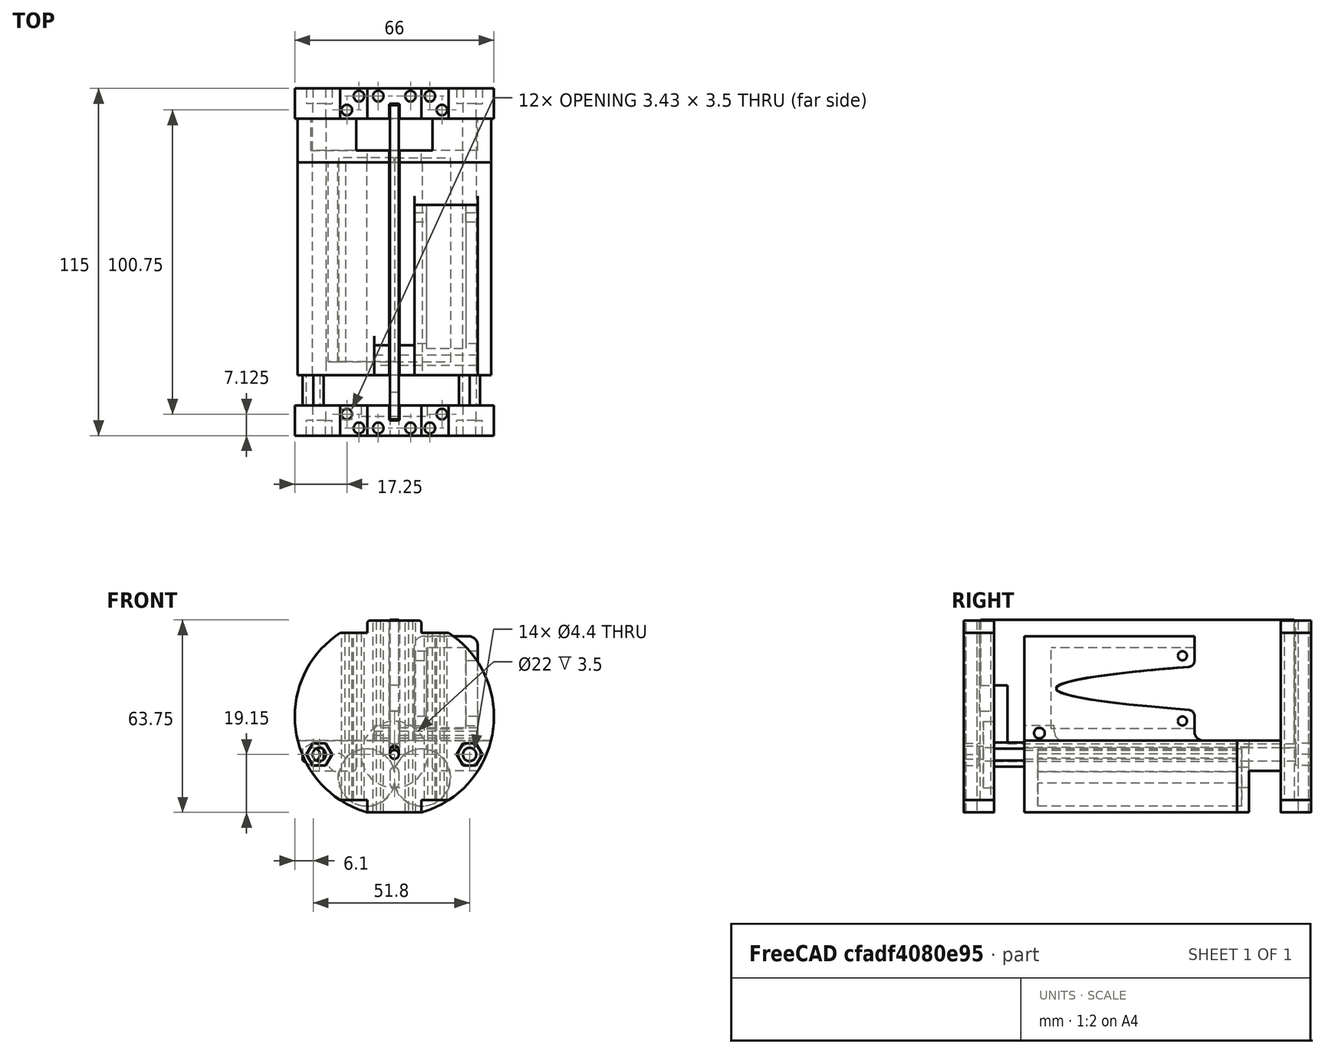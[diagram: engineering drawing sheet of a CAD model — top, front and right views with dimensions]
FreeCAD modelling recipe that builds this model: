
FCSTD DOCUMENT  (FreeCAD 0.19R24366 (Git))
Label: Corte_piezas_DEF_3
License: Creative Commons Attribution-ShareAlike
LicenseURL: http://creativecommons.org/licenses/by-sa/4.0/
objects: Sketcher::SketchObject×25, PartDesign::Pocket×14, PartDesign::Fillet×12, PartDesign::Pad×11, TechDraw::DrawViewDimension×9, PartDesign::Body×7, PartDesign::ShapeBinder×6, PartDesign::Mirrored×5, TechDraw::DrawViewPart×2, TechDraw::DrawSVGTemplate×2, TechDraw::DrawPage×2, Spreadsheet::Sheet×1, PartDesign::MultiTransform×1
note: 118 computed .brp shape members not serialized (recipe doc carries the construction recipe); baked Part::Feature solids carry a one-line shape summary decoded from their .brp

FEATURE [Spreadsheet::Sheet] Spreadsheet  label="Datos"
  cells = A1=Diámetro pila; B1(DiametroPila)=18.5; A2=Tolerancia; B2(tolerancia)=0.4; A3=Largo Pila; B3(largoPila)=65; A4=Separacion; B4(separacion)=1; A5=Grosor tapa; B5(grosortapa)=4.5; A6=Largo Bote; B6(LargoBote)=115; A7= Rosca pasante Diámetro; B7(roscaPasante4)=4; A8=Ancho placa electrónica; B8(anchoPlaca)=3; A9=Diámetro tornillos placa; B9(tornillosParaLaPlaca)=3; A10=GrosorGPS; B10(GPSgrosor)=12.5; A11=AnchoGPS; B11(GPSancho)=26.2; A12=AltoGPS; B12(GPSAlto)=36
FEATURE [Sketcher::SketchObject] Sketch  label="habitaculo_pila_antena"
  FullyConstrained = true
  MapMode = 5
  Placement = pos=(0,0,0) rot=(1,0,0;1.5708rad)
  Support = -> [XZ_Plane]
  expr: Constraints[7] = <<Datos>>.tolerancia + <<Datos>>.roscaPasante4
  expr: Constraints[2] = <<Datos>>.DiametroPila + <<Datos>>.tolerancia
  expr: Constraints[15] = <<Datos>>.DiametroPila
  sketch-geometry (13):
    g0: Circle CenterX=0 CenterY=0 CenterZ=0 NormalX=0 NormalY=0 NormalZ=1 AngleXU=0 Radius=33
    g1: LineSegment StartX=-9.25 StartY=-31.6771 StartZ=0 EndX=9.25 EndY=-31.6771 EndZ=0
    g2: LineSegment StartX=-32.0156 StartY=-8 StartZ=0 EndX=32.0156 EndY=-8 EndZ=0
    g3: ArcOfCircle CenterX=-9.25 CenterY=-20.1771 CenterZ=0 NormalX=0 NormalY=0 NormalZ=1 AngleXU=0 Radius=9.45 StartAngle=0.206102 EndAngle=2.40475
    g4: ArcOfCircle CenterX=9.25 CenterY=-20.1771 CenterZ=0 NormalX=0 NormalY=0 NormalZ=1 AngleXU=0 Radius=9.45 StartAngle=3.3477 EndAngle=9.21868
    g5: Circle CenterX=24.9 CenterY=-12.6 CenterZ=0 NormalX=0 NormalY=0 NormalZ=1 AngleXU=0 Radius=2.2
    g6: ArcOfCircle CenterX=0 CenterY=0 CenterZ=0 NormalX=0 NormalY=0 NormalZ=1 AngleXU=0 Radius=33 StartAngle=3.38646 EndAngle=4.42828
    g7: ArcOfCircle CenterX=0 CenterY=0 CenterZ=0 NormalX=0 NormalY=0 NormalZ=1 AngleXU=0 Radius=33 StartAngle=4.9965 EndAngle=6.03832
    g8: ArcOfCircle CenterX=-18.8935 CenterY=-15.243 CenterZ=0 NormalX=0 NormalY=0 NormalZ=1 AngleXU=0 Radius=3 StartAngle=0.491509 EndAngle=4.84582
    g9: ArcOfCircle CenterX=-9.25 CenterY=-20.1771 CenterZ=0 NormalX=0 NormalY=0 NormalZ=1 AngleXU=0 Radius=9.45 StartAngle=2.93258 EndAngle=6.07708
    g10: Circle CenterX=-24.9 CenterY=-12.6 CenterZ=0 NormalX=0 NormalY=0 NormalZ=1 AngleXU=0 Radius=2.2
    g11: Circle CenterX=0 CenterY=-12.6 CenterZ=0 NormalX=0 NormalY=0 NormalZ=1 AngleXU=0 Radius=1.45
    g12: LineSegment StartX=24.9 StartY=-12.6 StartZ=0 EndX=0 EndY=-12.6 EndZ=0
  constraints (38):
    c: Diameter(g0) = 66
    c: Horizontal(g1)
    c: Diameter(g3) = 18.9
    c: Equal(g3,g4)
    c: Coincident(g4,g9)
    c: Coincident(g4,g3)
    c: Coincident(g0,g-1)
    c: Diameter(g5) = 4.4
    c: Horizontal(g2)
    c: Vertical(g1,g4)
    c: Coincident(g6,g-1)
    c: Coincident(g6,g1)
    c: Coincident(g7,g6)
    c: Coincident(g7,g1)
    c: Symmetric(g4,g3,g-2)
    c: DistanceX(g3,g4) = 18.5
    c: PointOnObject(g1,g0)
    c: DistanceY(g1,g3) = 11.5
    c: DistanceY(g2,g6) = 8
    c: PointOnObject(g6,g0)
    c: Coincident(g2,g6)
    c: Coincident(g7,g2)
    c: Equal(g3,g9)
    c: Coincident(g3,g8)
    c: Coincident(g9,g8)
    c: Coincident(g3,g9)
    c: Radius(g8) = 3
    c: DistanceX(g8,g2) = -13.1222
    c: DistanceY(g8,g2) = 7.24297
    c: Symmetric(g10,g5,g-2)
    c: Equal(g10,g5)
    c: Diameter(g11) = 2.9  'Antena'
    c: Coincident(g12,g5)
    c: Coincident(g12,g11)
    c: Horizontal(g12)
    c: PointOnObject(g11,g-2)
    c: DistanceY(g5,g2) = 4.6
    c: DistanceX(g11,g5) = 24.9
FEATURE [PartDesign::Pad] Pad  label="habitaculo_Pila"
  Direction = (1,1,1)
  Length = 66
  Length2 = 100
  Midplane = true
  Placement = pos=(0,0,0) rot=(1,0,0;1.5708rad)
  Profile = -> Sketch
  Type = 0
  expr: Length = <<Datos>>.largoPila + <<Datos>>.separacion
FEATURE [PartDesign::ShapeBinder] ShapeBinder003
  Placement = pos=(0,-4.5,-1e-15) rot=(0,0,1;0rad)
  TraceSupport = false
FEATURE [Sketcher::SketchObject] Sketch022  label="Sketch_placa"
  ExternalGeometry = -> [ShapeBinder003]
  FullyConstrained = true
  Placement = pos=(0,0,-3.7e-14) rot=(0,0.707107,0.707107;3.14159rad)
  Support = -> [ShapeBinder003]
  expr: Constraints[8] = <<Datos>>.anchoPlaca
  sketch-geometry (4):
    g0: LineSegment StartX=-1.5 StartY=32 StartZ=0 EndX=1.5 EndY=32 EndZ=0
    g1: LineSegment StartX=1.5 StartY=32 StartZ=0 EndX=1.5 EndY=-9 EndZ=0
    g2: LineSegment StartX=1.5 StartY=-9 StartZ=0 EndX=-1.5 EndY=-9 EndZ=0
    g3: LineSegment StartX=-1.5 StartY=-9 StartZ=0 EndX=-1.5 EndY=32 EndZ=0
  constraints (11):
    c: Coincident(g0,g1)
    c: Coincident(g1,g2)
    c: Coincident(g2,g3)
    c: Coincident(g3,g0)
    c: Horizontal(g2)
    c: Vertical(g1)
    c: Vertical(g3)
    c: Symmetric(g0,g0,g-2)
    c: DistanceX(g0,g0) = 3
    c: DistanceY(g1,g1) = 41
    c: DistanceY(g-3,g0) = 40
FEATURE [PartDesign::Pad] Pad009  label="Placa_electrónica"
  Direction = (1,1,1)
  Length = 104
  Length2 = 100
  Midplane = true
  Placement = pos=(0,-4.5,-1e-15) rot=(0,0,1;0rad)
  Profile = -> Sketch022
  Type = 0
FEATURE [Sketcher::SketchObject] Sketch023
  ExternalGeometry = -> [Pad009]
  FullyConstrained = true
  MapMode = 5
  Placement = pos=(0,-52,5.17e-14) rot=(1,0,0;1.5708rad)
  Support = -> [Pad009]
  sketch-geometry (4):
    g0: LineSegment StartX=-1.5 StartY=-9 StartZ=0 EndX=1.5 EndY=-9 EndZ=0
    g1: LineSegment StartX=1.5 StartY=-9 StartZ=0 EndX=1.5 EndY=10.3 EndZ=0
    g2: LineSegment StartX=1.5 StartY=10.3 StartZ=0 EndX=-1.5 EndY=10.3 EndZ=0
    g3: LineSegment StartX=-1.5 StartY=10.3 StartZ=0 EndX=-1.5 EndY=-9 EndZ=0
  constraints (11):
    c: Coincident(g0,g1)
    c: Coincident(g1,g2)
    c: Coincident(g2,g3)
    c: Coincident(g3,g0)
    c: Horizontal(g0)
    c: Horizontal(g2)
    c: Vertical(g1)
    c: Vertical(g3)
    c: Coincident(g0,g-3)
    c: PointOnObject(g1,g-4)
    c: DistanceY(g1,g1) = 19.3
FEATURE [PartDesign::Pocket] Pocket011
  BaseFeature = -> Pad009
  Length = 9
  Length2 = 100
  Placement = pos=(0,-4.5,-1e-15) rot=(0,0,1;0rad)
  Profile = -> Sketch023
  Type = 0
FEATURE [PartDesign::Body] Body003  label="Placa_electronica"
  Group = -> [ShapeBinder003,Sketch022,Pad009,Sketch023,Pocket011]
  Origin = -> Origin003
  Tip = -> Pocket011
FEATURE [PartDesign::ShapeBinder] ShapeBinder
  Placement = pos=(0,-4.5,-1e-15) rot=(0,0,1;0rad)
  TraceSupport = false
FEATURE [Sketcher::SketchObject] Sketch024  label="Forma_pasante1"
  ExternalGeometry = -> [ShapeBinder]
  FullyConstrained = true
  MapMode = 5
  Placement = pos=(0,-37.5,-1.19e-14) rot=(1,0,0;1.5708rad)
  Support = -> [ShapeBinder]
  sketch-geometry (8):
    g0: Circle CenterX=24.9 CenterY=-12.6 CenterZ=0 NormalX=0 NormalY=0 NormalZ=1 AngleXU=0 Radius=2.2
    g1: LineSegment StartX=28.3641 StartY=-14.6 StartZ=0 EndX=28.3641 EndY=-10.6 EndZ=0
    g2: LineSegment StartX=28.3641 StartY=-10.6 StartZ=0 EndX=24.9 EndY=-8.6 EndZ=0
    g3: LineSegment StartX=24.9 StartY=-8.6 StartZ=0 EndX=21.4359 EndY=-10.6 EndZ=0
    g4: LineSegment StartX=21.4359 StartY=-10.6 StartZ=0 EndX=21.4359 EndY=-14.6 EndZ=0
    g5: LineSegment StartX=21.4359 StartY=-14.6 StartZ=0 EndX=24.9 EndY=-16.6 EndZ=0
    g6: LineSegment StartX=24.9 StartY=-16.6 StartZ=0 EndX=28.3641 EndY=-14.6 EndZ=0
    g7: Circle CenterX=24.9 CenterY=-12.6 CenterZ=0 NormalX=0 NormalY=0 NormalZ=1 AngleXU=0 Radius=4
  constraints (18):
    c: Coincident(g0,g-3)
    c: Equal(g0,g-3)
    c: Coincident(g1,g2)
    c: Coincident(g2,g3)
    c: Coincident(g3,g4)
    c: Coincident(g4,g5)
    c: Coincident(g5,g6)
    c: Coincident(g6,g1)
    c: Equal(g1, g2-g6) x5
    c: PointOnObject(g1,g7)
    c: PointOnObject(g2,g7)
    c: PointOnObject(g3,g7)
    c: PointOnObject(g4,g7)
    c: PointOnObject(g5,g7)
    c: PointOnObject(g6,g7)
    c: Coincident(g7,g0)
    c: Vertical(g1)
    c: Distance(g2) = 4
FEATURE [PartDesign::Pad] Pad010
  Direction = (1,1,1)
  Length = 10
  Length2 = 100
  Placement = pos=(0,-4.5,-1e-15) rot=(0,0,1;0rad)
  Profile = -> Sketch024
  Type = 0
FEATURE [PartDesign::Body] Body004  label="Pasante1"
  Group = -> [ShapeBinder,Sketch024,Pad010]
  Origin = -> Origin004
  Tip = -> Pad010
FEATURE [PartDesign::ShapeBinder] ShapeBinder004
  Placement = pos=(0,-10,-2.2e-15) rot=(0,0,1;0rad)
  Support = -> [Pad010]
  TraceSupport = false
FEATURE [Sketcher::SketchObject] Sketch025
  ExternalGeometry = -> [ShapeBinder004]
  FullyConstrained = true
  MapMode = 5
  Placement = pos=(0,-47.5,-2.43e-14) rot=(1,0,0;1.5708rad)
  Support = -> [ShapeBinder004]
  sketch-geometry (8):
    g0: Circle CenterX=24.9 CenterY=-12.6 CenterZ=0 NormalX=0 NormalY=0 NormalZ=1 AngleXU=0 Radius=2.2
    g1: LineSegment StartX=28.3641 StartY=-10.6 StartZ=0 EndX=24.9 EndY=-8.6 EndZ=0
    g2: LineSegment StartX=24.9 StartY=-8.6 StartZ=0 EndX=21.4359 EndY=-10.6 EndZ=0
    g3: LineSegment StartX=21.4359 StartY=-10.6 StartZ=0 EndX=21.4359 EndY=-14.6 EndZ=0
    g4: LineSegment StartX=21.4359 StartY=-14.6 StartZ=0 EndX=24.9 EndY=-16.6 EndZ=0
    g5: LineSegment StartX=24.9 StartY=-16.6 StartZ=0 EndX=28.3641 EndY=-14.6 EndZ=0
    g6: LineSegment StartX=28.3641 StartY=-14.6 StartZ=0 EndX=28.3641 EndY=-10.6 EndZ=0
    g7: Circle CenterX=24.9 CenterY=-12.6 CenterZ=0 NormalX=0 NormalY=0 NormalZ=1 AngleXU=0 Radius=4
  constraints (17):
    c: Coincident(g0,g-5)
    c: PointOnObject(g-4,g0)
    c: Coincident(g1,g2)
    c: Coincident(g2,g3)
    c: Coincident(g3,g4)
    c: Coincident(g4,g5)
    c: Coincident(g5,g6)
    c: Coincident(g6,g1)
    c: Equal(g1, g2-g6) x5
    c: PointOnObject(g1,g7)
    c: PointOnObject(g2,g7)
    c: PointOnObject(g3,g7)
    c: PointOnObject(g4,g7)
    c: PointOnObject(g5,g7)
    c: PointOnObject(g6,g7)
    c: Coincident(g7,g0)
    c: Coincident(g6,g-3)
FEATURE [PartDesign::Pad] Pad011
  Direction = (1,1,1)
  Length = 10
  Length2 = 100
  Placement = pos=(0,-10,-2.2e-15) rot=(0,0,1;0rad)
  Profile = -> Sketch025
  Type = 0
FEATURE [PartDesign::Body] Body005  label="Pasante2"
  Group = -> [ShapeBinder004,Sketch025,Pad011]
  Origin = -> Origin005
  Placement = pos=(-51.8,10,1.8e-15) rot=(0,0,1;0rad)
  Tip = -> Pad011
FEATURE [PartDesign::ShapeBinder] ShapeBinder005
  Placement = pos=(0,-4.5,-1e-15) rot=(0,0,1;0rad)
  TraceSupport = false
FEATURE [Sketcher::SketchObject] Sketch026
  ExternalGeometry = -> [ShapeBinder005]
  FullyConstrained = true
  Placement = pos=(0,-47.5,0) rot=(1,0,0;1.5708rad)
  Support = -> [ShapeBinder005]
  sketch-geometry (26):
    g0: ArcOfCircle CenterX=0 CenterY=0 CenterZ=0 NormalX=0 NormalY=0 NormalZ=1 AngleXU=0 Radius=33 StartAngle=5.28932 EndAngle=7.27705
    g1: LineSegment StartX=-9 StartY=-31.749 StartZ=0 EndX=9 EndY=-31.749 EndZ=0
    g2: LineSegment StartX=-9 StartY=31.749 StartZ=0 EndX=9 EndY=31.749 EndZ=0
    g3: ArcOfCircle CenterX=0 CenterY=0 CenterZ=0 NormalX=0 NormalY=0 NormalZ=1 AngleXU=0 Radius=33 StartAngle=2.14773 EndAngle=4.13546
    g4: ArcOfCircle CenterX=0 CenterY=-12.6 CenterZ=0 NormalX=0 NormalY=0 NormalZ=1 AngleXU=0 Radius=1.45 StartAngle=3.14159 EndAngle=6.28319
    g5: ArcOfCircle CenterX=1e-16 CenterY=-11.15 CenterZ=0 NormalX=0 NormalY=0 NormalZ=1 AngleXU=0 Radius=1.45 StartAngle=0 EndAngle=3.14159
    g6: LineSegment StartX=1.45 StartY=-12.6 StartZ=0 EndX=1.45 EndY=-11.15 EndZ=0
    g7: LineSegment StartX=-1.45 StartY=-12.6 StartZ=0 EndX=-1.45 EndY=-11.15 EndZ=0
    g8: LineSegment StartX=-18 StartY=27.6586 StartZ=0 EndX=-18 EndY=-27.6586 EndZ=0
    g9: LineSegment StartX=18 StartY=27.6586 StartZ=0 EndX=18 EndY=-27.6586 EndZ=0
    g10: LineSegment StartX=27.0362 StartY=-16.3 StartZ=0 EndX=29.1724 EndY=-12.6 EndZ=0
    g11: LineSegment StartX=29.1724 StartY=-12.6 StartZ=0 EndX=27.0362 EndY=-8.9 EndZ=0
    g12: LineSegment StartX=27.0362 StartY=-8.9 StartZ=0 EndX=22.7638 EndY=-8.9 EndZ=0
    g13: LineSegment StartX=22.7638 StartY=-8.9 StartZ=0 EndX=20.6276 EndY=-12.6 EndZ=0
    g14: LineSegment StartX=20.6276 StartY=-12.6 StartZ=0 EndX=22.7638 EndY=-16.3 EndZ=0
    g15: LineSegment StartX=22.7638 StartY=-16.3 StartZ=0 EndX=27.0362 EndY=-16.3 EndZ=0
    g16: Circle CenterX=24.9 CenterY=-12.6 CenterZ=0 NormalX=0 NormalY=0 NormalZ=1 AngleXU=0 Radius=4.27239
    g17: LineSegment StartX=22.7638 StartY=-8.9 StartZ=0 EndX=29.1724 EndY=-12.6 EndZ=0
    g18: LineSegment StartX=-18 StartY=27.6586 StartZ=0 EndX=-9 EndY=27.6586 EndZ=0
    g19: LineSegment StartX=-9 StartY=31.749 StartZ=0 EndX=-9 EndY=27.6586 EndZ=0
    g20: LineSegment StartX=-18 StartY=-27.6586 StartZ=0 EndX=-9 EndY=-27.6586 EndZ=0
    g21: LineSegment StartX=-9 StartY=-31.749 StartZ=0 EndX=-9 EndY=-27.6586 EndZ=0
    g22: LineSegment StartX=9 StartY=31.749 StartZ=0 EndX=9 EndY=27.6586 EndZ=0
    g23: LineSegment StartX=18 StartY=27.6586 StartZ=0 EndX=9 EndY=27.6586 EndZ=0
    g24: LineSegment StartX=9 StartY=-31.749 StartZ=0 EndX=9 EndY=-27.6586 EndZ=0
    g25: LineSegment StartX=18 StartY=-27.6586 StartZ=0 EndX=9 EndY=-27.6586 EndZ=0
  constraints (65):
    c: Coincident(g0,g-1)
    c: Coincident(g1,g-4)
    c: PointOnObject(g2,g0)
    c: Horizontal(g2)
    c: Equal(g0,g3)
    c: Coincident(g0,g3)
    c: Tangent(g4,g7) = 1.5708
    c: Tangent(g4,g6) = -1.5708
    c: Tangent(g6,g5) = -1.5708
    c: Tangent(g7,g5) = 1.5708
    c: Vertical(g6)
    c: Equal(g4,g5)
    c: Coincident(g4,g-6)
    c: PointOnObject(g4,g-6)
    c: PointOnObject(g5,g-6)
    c: Vertical(g8)
    c: Vertical(g9)
    c: Coincident(g10,g11)
    c: Coincident(g11,g12)
    c: Coincident(g12,g13)
    c: Coincident(g13,g14)
    c: Coincident(g14,g15)
    c: Coincident(g15,g10)
    c: Equal(g10, g11-g15) x5
    c: PointOnObject(g10,g16)
    c: PointOnObject(g11,g16)
    c: PointOnObject(g12,g16)
    c: PointOnObject(g13,g16)
    c: PointOnObject(g14,g16)
    c: PointOnObject(g15,g16)
    c: Coincident(g16,g-7)
    c: Coincident(g17,g12)
    c: Coincident(g17,g10)
    c: Distance(g17) = 7.4
    c: Horizontal(g15)
    c: Coincident(g19,g2)
    c: Coincident(g19,g18)
    c: Vertical(g19)
    c: Horizontal(g18)
    c: Coincident(g3,g8)
    c: Coincident(g20,g8)
    c: Coincident(g21,g1)
    c: Coincident(g21,g20)
    c: Vertical(g21)
    c: Horizontal(g20)
    c: Coincident(g3,g8)
    c: Vertical(g22)
    c: Coincident(g23,g9)
    c: Coincident(g23,g22)
    c: Coincident(g24,g1)
    c: Vertical(g24)
    c: Coincident(g25,g9)
    c: Coincident(g25,g24)
    c: Horizontal(g25)
    c: Horizontal(g23)
    c: Coincident(g0,g9)
    c: Coincident(g0,g9)
    c: Equal(g23,g18)
    c: Equal(g20,g25)
    c: Equal(g25,g23)
    c: Coincident(g22,g2)
    c: Coincident(g18,g3)
    c: PointOnObject(g0,g-3)
    c: Coincident(g1,g-3)
    c: DistanceX(g23,g23) = 9
FEATURE [PartDesign::Pad] Pad012  label="Cuerpo_principal"
  Direction = (1,1,1)
  Length = 10
  Length2 = 100
  Placement = pos=(0,-4.5,-1e-15) rot=(0,0,1;0rad)
  Profile = -> Sketch026
  Type = 0
FEATURE [Sketcher::SketchObject] Sketch027
  ExternalGeometry = -> [Pad012]
  FullyConstrained = true
  MapMode = 5
  Placement = pos=(0,-4.5,31.749) rot=(0,0,1;0rad)
  Support = -> [Pad012]
  sketch-geometry (4):
    g0: LineSegment StartX=-1.7 StartY=-48 StartZ=0 EndX=1.7 EndY=-48 EndZ=0
    g1: LineSegment StartX=1.7 StartY=-48 StartZ=0 EndX=1.7 EndY=-43 EndZ=0
    g2: LineSegment StartX=1.7 StartY=-43 StartZ=0 EndX=-1.7 EndY=-43 EndZ=0
    g3: LineSegment StartX=-1.7 StartY=-43 StartZ=0 EndX=-1.7 EndY=-48 EndZ=0
  constraints (11):
    c: Coincident(g0,g1)
    c: Coincident(g1,g2)
    c: Coincident(g2,g3)
    c: Coincident(g3,g0)
    c: Horizontal(g0)
    c: Vertical(g1)
    c: Vertical(g3)
    c: PointOnObject(g1,g-4)
    c: Symmetric(g1,g2,g-2)
    c: DistanceX(g0,g0) = 3.4
    c: DistanceY(g1,g1) = 5
FEATURE [PartDesign::Pocket] Pocket  label="Ranura_placa"
  BaseFeature = -> Pad012
  Length = 30
  Length2 = 100
  Placement = pos=(0,-4.5,-1e-15) rot=(0,0,1;0rad)
  Profile = -> Sketch027
  Type = 0
FEATURE [Sketcher::SketchObject] Sketch028  label="SK_agujeros_pasantes_paracaidas"
  ExternalGeometry = -> [Pocket]
  FullyConstrained = true
  MapMode = 5
  Placement = pos=(0,-4.5,31.749) rot=(0,0,1;0rad)
  Support = -> [Pocket]
  sketch-geometry (14):
    g0: LineSegment StartX=-1.7 StartY=-48 StartZ=0 EndX=-9 EndY=-48 EndZ=0
    g1: LineSegment StartX=-1.7 StartY=-48 StartZ=0 EndX=-9 EndY=-53 EndZ=0
    g2: LineSegment StartX=-6.07487 StartY=-48.75 StartZ=0 EndX=-4.62513 EndY=-48.75 EndZ=0
    g3: ArcOfCircle CenterX=-5.35 CenterY=-50.5 CenterZ=0 NormalX=0 NormalY=0 NormalZ=1 AngleXU=0 Radius=1.75 StartAngle=2.35619 EndAngle=7.06858
    g4: LineSegment StartX=-6.07487 StartY=-48.75 StartZ=0 EndX=-6.58744 EndY=-49.2626 EndZ=0
    g5: LineSegment StartX=-4.11256 StartY=-49.2626 StartZ=0 EndX=-4.62513 EndY=-48.75 EndZ=0
    g6: LineSegment StartX=-6.58744 StartY=-49.2626 StartZ=0 EndX=-4.11256 EndY=-49.2626 EndZ=0
    g7: Circle CenterX=-5.35 CenterY=-50.5 CenterZ=0 NormalX=0 NormalY=0 NormalZ=1 AngleXU=0 Radius=1.75
    g8: LineSegment StartX=4.62513 StartY=-48.75 StartZ=0 EndX=6.07487 EndY=-48.75 EndZ=0
    g9: ArcOfCircle CenterX=5.35 CenterY=-50.5 CenterZ=0 NormalX=0 NormalY=0 NormalZ=1 AngleXU=0 Radius=1.75 StartAngle=2.35619 EndAngle=7.06858
    g10: LineSegment StartX=4.62513 StartY=-48.75 StartZ=0 EndX=4.11256 EndY=-49.2626 EndZ=0
    g11: LineSegment StartX=6.58744 StartY=-49.2626 StartZ=0 EndX=6.07487 EndY=-48.75 EndZ=0
    g12: LineSegment StartX=4.11256 StartY=-49.2626 StartZ=0 EndX=6.58744 EndY=-49.2626 EndZ=0
    g13: Circle CenterX=5.35 CenterY=-50.5 CenterZ=0 NormalX=0 NormalY=0 NormalZ=1 AngleXU=0 Radius=1.75
  constraints (33):
    c: Coincident(g0,g-8)
    c: PointOnObject(g0,g-3)
    c: Horizontal(g0)
    c: Coincident(g1,g0)
    c: Coincident(g1,g-3)
    c: Horizontal(g2)
    c: Coincident(g4,g2)
    c: Coincident(g5,g2)
    c: Coincident(g6,g3)
    c: Horizontal(g6)
    c: Tangent(g4,g3) = -1.5708
    c: Tangent(g5,g3) = -1.5708
    c: Angle(g6,g4) = 0.785398
    c: Diameter(g3) = 3.5
    c: Symmetric(g0,g1,g3)
    c: Coincident(g7,g3)
    c: PointOnObject(g3,g7)
    c: Tangent(g7,g2)
    c: Coincident(g3,g6)
    c: Horizontal(g8)
    c: Coincident(g10,g8)
    c: Coincident(g11,g8)
    c: Coincident(g12,g9)
    c: Horizontal(g12)
    c: Tangent(g10,g9) = -1.5708
    c: Tangent(g11,g9) = -1.5708
    c: Angle(g12,g10) = 0.785398
    c: Equal(g3,g9) = 3.5
    c: Coincident(g13,g9)
    c: PointOnObject(g9,g13)
    c: Tangent(g13,g8)
    c: Coincident(g9,g12)
    c: Symmetric(g9,g3,g-2)
FEATURE [PartDesign::Pocket] Pocket012  label="agujeros_pasantes_paracaidas"
  BaseFeature = -> Pocket
  Length = 5
  Length2 = 100
  Placement = pos=(0,-4.5,-1e-15) rot=(0,0,1;0rad)
  Profile = -> Sketch028
  Type = 1
FEATURE [Sketcher::SketchObject] Sketch029
  ExternalGeometry = -> [Pocket012]
  FullyConstrained = true
  MapMode = 5
  Placement = pos=(0,-47.5,8.5e-15) rot=(0,0.707107,0.707107;3.14159rad)
  Support = -> [Pocket012]
  sketch-geometry (2):
    g0: Circle CenterX=0 CenterY=-12.6 CenterZ=0 NormalX=0 NormalY=0 NormalZ=1 AngleXU=0 Radius=11
    g1: Circle CenterX=0 CenterY=-12.6 CenterZ=0 NormalX=0 NormalY=0 NormalZ=1 AngleXU=0 Radius=4
  constraints (4):
    c: Coincident(g0,g-3)
    c: Diameter(g0) = 22
    c: Coincident(g1,g0)
    c: Diameter(g1) = 8
FEATURE [PartDesign::Pocket] Pocket013  label="Arandela_GND"
  BaseFeature = -> Pocket012
  Length = 3.5
  Length2 = 100
  Placement = pos=(0,-4.5,-1e-15) rot=(0,0,1;0rad)
  Profile = -> Sketch029
  Type = 0
FEATURE [Sketcher::SketchObject] Sketch030
  ExternalGeometry = -> [ShapeBinder005]
  FullyConstrained = true
  MapMode = 5
  Placement = pos=(0,-57.5,1.07e-14) rot=(1,0,0;1.5708rad)
  Support = -> [Pocket013]
  sketch-geometry (15):
    g0: LineSegment StartX=27.0362 StartY=-16.3 StartZ=0 EndX=29.1724 EndY=-12.6 EndZ=0
    g1: LineSegment StartX=29.1724 StartY=-12.6 StartZ=0 EndX=27.0362 EndY=-8.9 EndZ=0
    g2: LineSegment StartX=27.0362 StartY=-8.9 StartZ=0 EndX=22.7638 EndY=-8.9 EndZ=0
    g3: LineSegment StartX=22.7638 StartY=-8.9 StartZ=0 EndX=20.6276 EndY=-12.6 EndZ=0
    g4: LineSegment StartX=20.6276 StartY=-12.6 StartZ=0 EndX=22.7638 EndY=-16.3 EndZ=0
    g5: LineSegment StartX=22.7638 StartY=-16.3 StartZ=0 EndX=27.0362 EndY=-16.3 EndZ=0
    g6: Circle CenterX=24.9 CenterY=-12.6 CenterZ=0 NormalX=0 NormalY=0 NormalZ=1 AngleXU=0 Radius=4.27239
    g7: LineSegment StartX=-22.7638 StartY=-16.3 StartZ=0 EndX=-20.6276 EndY=-12.6 EndZ=0
    g8: LineSegment StartX=-20.6276 StartY=-12.6 StartZ=0 EndX=-22.7638 EndY=-8.9 EndZ=0
    g9: LineSegment StartX=-22.7638 StartY=-8.9 StartZ=0 EndX=-27.0362 EndY=-8.9 EndZ=0
    g10: LineSegment StartX=-27.0362 StartY=-8.9 StartZ=0 EndX=-29.1724 EndY=-12.6 EndZ=0
    g11: LineSegment StartX=-29.1724 StartY=-12.6 StartZ=0 EndX=-27.0362 EndY=-16.3 EndZ=0
    g12: LineSegment StartX=-27.0362 StartY=-16.3 StartZ=0 EndX=-22.7638 EndY=-16.3 EndZ=0
    g13: Circle CenterX=-24.9 CenterY=-12.6 CenterZ=0 NormalX=0 NormalY=0 NormalZ=1 AngleXU=0 Radius=4.27239
    g14: LineSegment StartX=22.7638 StartY=-8.9 StartZ=0 EndX=29.1724 EndY=-12.6 EndZ=0
  constraints (34):
    c: Coincident(g0,g1)
    c: Coincident(g1,g2)
    c: Coincident(g2,g3)
    c: Coincident(g3,g4)
    c: Coincident(g4,g5)
    c: Coincident(g5,g0)
    c: Equal(g0, g1-g5) x5
    c: PointOnObject(g0,g6)
    c: PointOnObject(g1,g6)
    c: PointOnObject(g2,g6)
    c: PointOnObject(g3,g6)
    c: PointOnObject(g4,g6)
    c: PointOnObject(g5,g6)
    c: Coincident(g6,g-3)
    c: Coincident(g7,g8)
    c: Coincident(g8,g9)
    c: Coincident(g9,g10)
    c: Coincident(g10,g11)
    c: Coincident(g11,g12)
    c: Coincident(g12,g7)
    c: Equal(g7, g8-g12) x5
    c: PointOnObject(g7,g13)
    c: PointOnObject(g8,g13)
    c: PointOnObject(g9,g13)
    c: PointOnObject(g10,g13)
    c: PointOnObject(g11,g13)
    c: PointOnObject(g12,g13)
    c: Coincident(g13,g-4)
    c: Coincident(g14,g2)
    c: Distance(g14) = 7.4
    c: Horizontal(g5)
    c: Coincident(g14,g0)
    c: Equal(g2,g9)
    c: Horizontal(g12)
FEATURE [PartDesign::Pocket] Pocket014  label="Encastro_tuercas"
  BaseFeature = -> Pocket013
  Length = 5
  Length2 = 100
  Placement = pos=(0,-4.5,-1e-15) rot=(0,0,1;0rad)
  Profile = -> Sketch030
  Type = 0
FEATURE [Sketcher::SketchObject] Sketch031
  ExternalGeometry = -> [Pocket014]
  FullyConstrained = true
  MapMode = 5
  Placement = pos=(0,-52.5,4.51e-14) rot=(1,0,0;1.5708rad)
  Support = -> [Pocket014]
  sketch-geometry (3):
    g0: Circle CenterX=24.9 CenterY=-12.6 CenterZ=0 NormalX=0 NormalY=0 NormalZ=1 AngleXU=0 Radius=4.27239
    g1: Circle CenterX=24.9 CenterY=-12.6 CenterZ=0 NormalX=0 NormalY=0 NormalZ=1 AngleXU=0 Radius=2.2
    g2: Circle CenterX=-24.9 CenterY=-12.6 CenterZ=0 NormalX=0 NormalY=0 NormalZ=1 AngleXU=0 Radius=2.2
  constraints (7):
    c: PointOnObject(g-8,g0)
    c: PointOnObject(g-4,g0)
    c: PointOnObject(g-5,g0)
    c: Coincident(g1,g0)
    c: Diameter(g1) = 4.4
    c: Equal(g1,g2) = 4.4
    c: Symmetric(g2,g1,g-2)
FEATURE [PartDesign::Pocket] Pocket015  label="Agujeros_pasantes_tornillos"
  BaseFeature = -> Pocket014
  Length = 5
  Length2 = 100
  Placement = pos=(0,-4.5,-1e-15) rot=(0,0,1;0rad)
  Profile = -> Sketch031
  Type = 1
FEATURE [Sketcher::SketchObject] Sketch032  label="SK_agujeros_pasantes_paracaidas_2"
  ExternalGeometry = -> [Pocket015]
  FullyConstrained = true
  MapMode = 5
  Placement = pos=(0,-4.5,27.6586) rot=(0,0,1;0rad)
  Support = -> [Pocket015]
  sketch-geometry (16):
    g0: LineSegment StartX=11.0251 StartY=-48.75 StartZ=0 EndX=12.4749 EndY=-48.75 EndZ=0
    g1: ArcOfCircle CenterX=11.75 CenterY=-50.5 CenterZ=0 NormalX=0 NormalY=0 NormalZ=1 AngleXU=0 Radius=1.75 StartAngle=2.35619 EndAngle=7.06858
    g2: LineSegment StartX=11.0251 StartY=-48.75 StartZ=0 EndX=10.5126 EndY=-49.2626 EndZ=0
    g3: LineSegment StartX=12.4749 StartY=-48.75 StartZ=0 EndX=12.9874 EndY=-49.2626 EndZ=0
    g4: LineSegment StartX=10.5126 StartY=-49.2626 StartZ=0 EndX=12.9874 EndY=-49.2626 EndZ=0
    g5: LineSegment StartX=6.07487 StartY=-48.75 StartZ=0 EndX=18 EndY=-48.75 EndZ=0
    g6: LineSegment StartX=13.5 StartY=-43 StartZ=0 EndX=13.5 EndY=-53 EndZ=0
    g7: ArcOfCircle CenterX=11.75 CenterY=-50.5 CenterZ=0 NormalX=0 NormalY=0 NormalZ=1 AngleXU=0 Radius=1.75 StartAngle=1.5708 EndAngle=2.35619
    g8: LineSegment StartX=15.0251 StartY=-44.125 StartZ=0 EndX=16.4749 EndY=-44.125 EndZ=0
    g9: ArcOfCircle CenterX=15.75 CenterY=-45.875 CenterZ=0 NormalX=0 NormalY=0 NormalZ=1 AngleXU=0 Radius=1.75 StartAngle=2.35619 EndAngle=7.06858
    g10: LineSegment StartX=15.0251 StartY=-44.125 StartZ=0 EndX=14.5126 EndY=-44.6376 EndZ=0
    g11: LineSegment StartX=16.4749 StartY=-44.125 StartZ=0 EndX=16.9874 EndY=-44.6376 EndZ=0
    g12: LineSegment StartX=14.5126 StartY=-44.6376 StartZ=0 EndX=16.9874 EndY=-44.6376 EndZ=0
    g13: ArcOfCircle CenterX=15.75 CenterY=-45.875 CenterZ=0 NormalX=0 NormalY=0 NormalZ=1 AngleXU=0 Radius=1.75 StartAngle=1.57079 EndAngle=2.35619
    g14: LineSegment StartX=13.5 StartY=-43 StartZ=0 EndX=18 EndY=-48.75 EndZ=0
    g15: LineSegment StartX=13.5 StartY=-48.75 StartZ=0 EndX=18 EndY=-43 EndZ=0
  constraints (43):
    c: Diameter(g1) = 3.5
    c: Coincident(g1,g4)
    c: Horizontal(g4)
    c: Coincident(g0,g2)
    c: Horizontal(g0)
    c: Coincident(g0,g3)
    c: PointOnObject(g5,g-3)
    c: Horizontal(g5)
    c: PointOnObject(g6,g-5)
    c: Vertical(g6)
    c: Symmetric(g-4,g-6,g6)
    c: Tangent(g1,g2) = -1.5708
    c: Tangent(g3,g1) = 1.5708
    c: Coincident(g4,g1)
    c: Coincident(g7,g1)
    c: Coincident(g7,g1)
    c: Tangent(g0,g7)
    c: Angle(g4,g2) = 0.785398
    c: PointOnObject(g7,g0)
    c: Coincident(g5,g-7)
    c: Diameter(g9) = 3.5
    c: Coincident(g9,g12)
    c: Horizontal(g12)
    c: Coincident(g8,g10)
    c: Horizontal(g8)
    c: Coincident(g8,g11)
    c: Tangent(g9,g10) = -1.5708
    c: Tangent(g11,g9) = 1.5708
    c: Coincident(g12,g9)
    c: Coincident(g13,g9)
    c: Coincident(g13,g9)
    c: Tangent(g8,g13)
    c: Angle(g12,g10) = 0.785398
    c: PointOnObject(g13,g8)
    c: Coincident(g14,g6)
    c: Coincident(g14,g5)
    c: PointOnObject(g9,g14)
    c: PointOnObject(g15,g6)
    c: Coincident(g15,g-4)
    c: PointOnObject(g9,g15)
    c: PointOnObject(g15,g5)
    c: PointOnObject(g0,g5)
    c: Tangent(g1,g6)
FEATURE [PartDesign::Pocket] Pocket016  label="Agujeros_pasantes_paracaidas_2"
  BaseFeature = -> Pocket015
  Length = 5
  Length2 = 100
  Placement = pos=(0,-4.5,-1e-15) rot=(0,0,1;0rad)
  Profile = -> Sketch032
  Type = 1
FEATURE [PartDesign::Mirrored] Mirrored  label="Con_todos_agujeros_pasantes"
  BaseFeature = -> Pocket016
  MirrorPlane = -> Sketch032 [V_Axis]
  Originals = -> [Pocket016]
  Placement = pos=(0,-4.5,-1e-15) rot=(0,0,1;0rad)
FEATURE [PartDesign::Fillet] Fillet
  Base = -> Mirrored [Edge123,Edge109]
  BaseFeature = -> Mirrored
  Placement = pos=(0,-4.5,-1e-15) rot=(0,0,1;0rad)
  Radius = 0.5
  SupportTransform = false
FEATURE [PartDesign::Fillet] Fillet001
  Base = -> Fillet [Edge5,Edge9]
  BaseFeature = -> Fillet
  Placement = pos=(0,-4.5,-1e-15) rot=(0,0,1;0rad)
  Radius = 1
  SupportTransform = false
FEATURE [PartDesign::Fillet] Fillet002
  Base = -> Fillet001 [Edge114,Edge115]
  BaseFeature = -> Fillet001
  Placement = pos=(0,-4.5,-1e-15) rot=(0,0,1;0rad)
  Radius = 1
  SupportTransform = false
FEATURE [PartDesign::Body] Body006  label="LateralA"
  Group = -> [ShapeBinder005,Sketch026,Pad012,Sketch027,Pocket,Sketch028,Pocket012,Sketch029,Pocket013,Sketch030,Pocket014,Sketch031,Pocket015,Sketch032,Pocket016,Mirrored,Fillet,Fillet001,Fillet002]
  Origin = -> Origin006
  Tip = -> Fillet002
FEATURE [PartDesign::ShapeBinder] ShapeBinder006
  Placement = pos=(0,33,7e-15) rot=(0,0,1;0rad)
  TraceSupport = false
FEATURE [Sketcher::SketchObject] Sketch033
  ExternalGeometry = -> [ShapeBinder006]
  FullyConstrained = true
  MapMode = 5
  Placement = pos=(0,33,7e-15) rot=(0,0.707107,0.707107;3.14159rad)
  Support = -> [ShapeBinder006]
  sketch-geometry (10):
    g0: ArcOfCircle CenterX=1.2e-15 CenterY=0 CenterZ=0 NormalX=0 NormalY=0 NormalZ=1 AngleXU=0 Radius=33 StartAngle=4.98862 EndAngle=6.03832
    g1: ArcOfCircle CenterX=1.2e-15 CenterY=0 CenterZ=0 NormalX=0 NormalY=0 NormalZ=1 AngleXU=0 Radius=33 StartAngle=3.38646 EndAngle=4.43616
    g2: LineSegment StartX=-32.0156 StartY=-8 StartZ=0 EndX=32.0156 EndY=-8 EndZ=0
    g3: LineSegment StartX=9 StartY=-31.749 StartZ=0 EndX=-9 EndY=-31.749 EndZ=0
    g4: ArcOfCircle CenterX=0 CenterY=-18.3411 CenterZ=0 NormalX=0 NormalY=0 NormalZ=1 AngleXU=0 Radius=1.5 StartAngle=9e-16 EndAngle=3.14159
    g5: ArcOfCircle CenterX=0 CenterY=-22.1569 CenterZ=0 NormalX=0 NormalY=0 NormalZ=1 AngleXU=0 Radius=1.5 StartAngle=3.14159 EndAngle=6.28319
    g6: LineSegment StartX=-1.5 StartY=-18.3411 StartZ=0 EndX=-1.5 EndY=-22.1569 EndZ=0
    g7: LineSegment StartX=1.5 StartY=-18.3411 StartZ=0 EndX=1.5 EndY=-22.1569 EndZ=0
    g8: Circle CenterX=24.9 CenterY=-12.6 CenterZ=0 NormalX=0 NormalY=0 NormalZ=1 AngleXU=0 Radius=2.2
    g9: Circle CenterX=-24.9 CenterY=-12.6 CenterZ=0 NormalX=0 NormalY=0 NormalZ=1 AngleXU=0 Radius=2.2
  constraints (21):
    c: Coincident(g0,g-3)
    c: Coincident(g0,g-4)
    c: Coincident(g1,g0)
    c: Coincident(g1,g-3)
    c: Coincident(g1,g-4)
    c: Coincident(g2,g1)
    c: Coincident(g2,g0)
    c: Coincident(g3,g0)
    c: Coincident(g3,g1)
    c: Tangent(g4,g7) = 1.5708
    c: Tangent(g4,g6) = -1.5708
    c: Tangent(g6,g5) = -1.5708
    c: Tangent(g7,g5) = 1.5708
    c: Vertical(g6)
    c: Coincident(g4,g-5)
    c: Coincident(g5,g-6)
    c: Diameter(g4) = 3
    c: Coincident(g8,g-8)
    c: Equal(g8,g-7)
    c: Coincident(g9,g-7)
    c: Equal(g9,g-7)
FEATURE [PartDesign::Pad] Pad013  label="tapa_pilas"
  Direction = (1,1,1)
  Length = 4
  Length2 = 100
  Placement = pos=(0,33,7e-15) rot=(0,0,1;0rad)
  Profile = -> Sketch033
  Type = 0
FEATURE [Sketcher::SketchObject] Sketch034
  ExternalGeometry = -> [Pad013]
  FullyConstrained = true
  MapMode = 5
  Placement = pos=(0,37,8.3e-15) rot=(0,0.707107,0.707107;3.14159rad)
  Support = -> [Pad013]
  sketch-geometry (10):
    g0: ArcOfCircle CenterX=0 CenterY=0 CenterZ=0 NormalX=0 NormalY=0 NormalZ=1 AngleXU=0 Radius=33 StartAngle=3.38646 EndAngle=3.71852
    g1: LineSegment StartX=-27.6586 StartY=-18 StartZ=0 EndX=-12.6586 EndY=-18 EndZ=0
    g2: LineSegment StartX=-12.6586 StartY=-18 StartZ=0 EndX=-12.6586 EndY=-8 EndZ=0
    g3: LineSegment StartX=-32.0156 StartY=-8 StartZ=0 EndX=-12.6586 EndY=-8 EndZ=0
    g4: Circle CenterX=-24.9 CenterY=-12.6 CenterZ=0 NormalX=0 NormalY=0 NormalZ=1 AngleXU=0 Radius=2.2
    g5: ArcOfCircle CenterX=-5.1e-15 CenterY=-8.1e-15 CenterZ=0 NormalX=0 NormalY=0 NormalZ=1 AngleXU=0 Radius=33 StartAngle=5.70625 EndAngle=6.03832
    g6: LineSegment StartX=27.6586 StartY=-18 StartZ=0 EndX=12.6586 EndY=-18 EndZ=0
    g7: LineSegment StartX=12.6586 StartY=-18 StartZ=0 EndX=12.6586 EndY=-8 EndZ=0
    g8: LineSegment StartX=32.0156 StartY=-8 StartZ=0 EndX=12.6586 EndY=-8 EndZ=0
    g9: Circle CenterX=24.9 CenterY=-12.6 CenterZ=0 NormalX=0 NormalY=0 NormalZ=1 AngleXU=0 Radius=2.2
  constraints (24):
    c: Coincident(g0,g-1)
    c: Coincident(g0,g-3)
    c: Coincident(g1,g0)
    c: Horizontal(g1)
    c: PointOnObject(g2,g-3)
    c: Vertical(g2)
    c: Coincident(g2,g1)
    c: Coincident(g3,g0)
    c: Coincident(g3,g2)
    c: DistanceY(g2,g2) = 10
    c: DistanceX(g1,g1) = 15
    c: Coincident(g4,g-4)
    c: Equal(g-4,g4)
    c: Coincident(g6,g5)
    c: Coincident(g7,g6)
    c: Coincident(g8,g5)
    c: Coincident(g8,g7)
    c: Symmetric(g7,g2,g-2)
    c: Symmetric(g6,g1,g-2)
    c: Symmetric(g5,g0,g-2)
    c: Symmetric(g9,g4,g-2)
    c: Equal(g9,g4)
    c: Equal(g5,g0)
    c: Symmetric(g5,g0,g-2)
FEATURE [PartDesign::Pad] Pad014
  BaseFeature = -> Pad013
  Direction = (1,1,1)
  Length = 10.5
  Length2 = 100
  Placement = pos=(0,33,7e-15) rot=(0,0,1;0rad)
  Profile = -> Sketch034
  Type = 0
FEATURE [PartDesign::Fillet] Fillet003
  Base = -> Pad014 [Edge51,Edge48]
  BaseFeature = -> Pad014
  Placement = pos=(0,33,7e-15) rot=(0,0,1;0rad)
  Radius = 1
  SupportTransform = false
FEATURE [PartDesign::ShapeBinder] ShapeBinder007
  TraceSupport = false
FEATURE [Sketcher::SketchObject] Sketch035
  ExternalGeometry = -> [ShapeBinder007]
  FullyConstrained = true
  MapMode = 5
  Placement = pos=(0,-47.5,1.04e-14) rot=(0,0.707107,0.707107;3.14159rad)
  Support = -> [ShapeBinder007]
  sketch-geometry (14):
    g0: ArcOfCircle CenterX=0 CenterY=-1.2e-14 CenterZ=0 NormalX=0 NormalY=0 NormalZ=1 AngleXU=0 Radius=33 StartAngle=2.14773 EndAngle=4.13546
    g1: ArcOfCircle CenterX=0 CenterY=-1.2e-14 CenterZ=0 NormalX=0 NormalY=0 NormalZ=1 AngleXU=0 Radius=33 StartAngle=5.28932 EndAngle=7.27705
    g2: LineSegment StartX=-18 StartY=27.6586 StartZ=0 EndX=-9 EndY=27.6586 EndZ=0
    g3: LineSegment StartX=9 StartY=27.6586 StartZ=0 EndX=18 EndY=27.6586 EndZ=0
    g4: LineSegment StartX=-9 StartY=27.6586 StartZ=0 EndX=-9 EndY=31.749 EndZ=0
    g5: LineSegment StartX=9 StartY=27.6586 StartZ=0 EndX=9 EndY=31.749 EndZ=0
    g6: LineSegment StartX=-9 StartY=31.749 StartZ=0 EndX=9 EndY=31.749 EndZ=0
    g7: LineSegment StartX=-9 StartY=-27.6586 StartZ=0 EndX=-9 EndY=-31.749 EndZ=0
    g8: LineSegment StartX=9 StartY=-27.6586 StartZ=0 EndX=9 EndY=-31.749 EndZ=0
    g9: LineSegment StartX=9 StartY=-27.6586 StartZ=0 EndX=18 EndY=-27.6586 EndZ=0
    g10: LineSegment StartX=-18 StartY=-27.6586 StartZ=0 EndX=-9 EndY=-27.6586 EndZ=0
    g11: LineSegment StartX=-9 StartY=-31.749 StartZ=0 EndX=9 EndY=-31.749 EndZ=0
    g12: Circle CenterX=-24.9 CenterY=-12.6 CenterZ=0 NormalX=0 NormalY=0 NormalZ=1 AngleXU=0 Radius=2.2
    g13: Circle CenterX=24.9 CenterY=-12.6 CenterZ=0 NormalX=0 NormalY=0 NormalZ=1 AngleXU=0 Radius=2.2
  constraints (34):
    c: Coincident(g0,g-5)
    c: Coincident(g0,g-7)
    c: Coincident(g1,g0)
    c: Coincident(g1,g-6)
    c: Coincident(g1,g-9)
    c: Coincident(g2,g0)
    c: Coincident(g2,g-5)
    c: Coincident(g3,g-6)
    c: Coincident(g3,g1)
    c: Coincident(g4,g2)
    c: Vertical(g4)
    c: Coincident(g5,g3)
    c: Vertical(g5)
    c: Coincident(g6,g4)
    c: Coincident(g6,g5)
    c: Horizontal(g6)
    c: PointOnObject(g-3,g6)
    c: Coincident(g7,g-7)
    c: Vertical(g7)
    c: Coincident(g8,g-9)
    c: Vertical(g8)
    c: Coincident(g9,g8)
    c: Coincident(g9,g1)
    c: Coincident(g10,g0)
    c: Coincident(g10,g7)
    c: Coincident(g11,g7)
    c: Coincident(g11,g8)
    c: Horizontal(g11)
    c: PointOnObject(g-8,g11)
    c: Coincident(g12,g-10)
    c: Coincident(g13,g-11)
    c: Equal(g12,g13)
    c: Equal(g13,g-11)
    c: Coincident(g0,g-1)
FEATURE [PartDesign::Pad] Pad015
  Direction = (1,1,1)
  Length = 10
  Length2 = 100
  Profile = -> Sketch035
  Reversed = true
  Type = 0
FEATURE [Sketcher::SketchObject] Sketch036
  ExternalGeometry = -> [Pad015]
  FullyConstrained = true
  MapMode = 5
  Placement = pos=(0,-47.5,1.04e-14) rot=(0,0.707107,0.707107;3.14159rad)
  Support = -> [Pad015]
  sketch-geometry (4):
    g0: LineSegment StartX=-1.7 StartY=31.749 StartZ=0 EndX=1.7 EndY=31.749 EndZ=0
    g1: LineSegment StartX=1.7 StartY=31.749 StartZ=0 EndX=1.7 EndY=-10.351 EndZ=0
    g2: LineSegment StartX=1.7 StartY=-10.351 StartZ=0 EndX=-1.7 EndY=-10.351 EndZ=0
    g3: LineSegment StartX=-1.7 StartY=-10.351 StartZ=0 EndX=-1.7 EndY=31.749 EndZ=0
  constraints (11):
    c: Coincident(g0,g1)
    c: Coincident(g1,g2)
    c: Coincident(g2,g3)
    c: Coincident(g3,g0)
    c: Horizontal(g2)
    c: Vertical(g1)
    c: Vertical(g3)
    c: PointOnObject(g0,g-3)
    c: Symmetric(g0,g0,g-2)
    c: DistanceX(g0,g0) = 3.4
    c: DistanceY(g1,g1) = 42.1
FEATURE [PartDesign::Pocket] Pocket017
  BaseFeature = -> Pad015
  Length = 5
  Length2 = 100
  Profile = -> Sketch036
  Type = 0
FEATURE [PartDesign::Mirrored] Mirrored001
  BaseFeature = -> Pocket017
  MirrorPlane = -> Sketch028 [V_Axis]
  Originals = -> [Pocket012]
FEATURE [PartDesign::Mirrored] Mirrored002
  MirrorPlane = -> Sketch032 [V_Axis]
FEATURE [PartDesign::Mirrored] Mirrored003
  MirrorPlane = -> Sketch032 [V_Axis]
FEATURE [PartDesign::MultiTransform] MultiTransform
  BaseFeature = -> Mirrored001
  Originals = -> [Pocket016]
  Transformations = -> [Mirrored002,Mirrored003]
FEATURE [PartDesign::Mirrored] Mirrored004
  BaseFeature = -> MultiTransform
  MirrorPlane = -> Sketch030 [V_Axis]
  Originals = -> [Pocket014]
FEATURE [PartDesign::Fillet] Fillet004
  Base = -> Mirrored004 [Edge85,Edge88]
  BaseFeature = -> Mirrored004
  Radius = 0.5
  SupportTransform = false
FEATURE [PartDesign::Fillet] Fillet005
  Base = -> Fillet004 [Edge9,Edge5,Edge113,Edge114]
  BaseFeature = -> Fillet004
  Radius = 1
  SupportTransform = false
FEATURE [PartDesign::Body] Body009  label="LateralB"
  Group = -> [ShapeBinder007,Sketch035,Pad015,Sketch036,Pocket017,Mirrored001,MultiTransform,Mirrored002,Mirrored003,Mirrored004,Fillet004,Fillet005]
  Origin = -> Origin009
  Placement = pos=(0,0,0) rot=(0,0,1;3.14159rad)
  Tip = -> Fillet005
FEATURE [Sketcher::SketchObject] Sketch037
  ExternalGeometry = -> [Pad]
  FullyConstrained = true
  MapMode = 5
  Placement = pos=(0,-33,-7e-15) rot=(1,0,0;1.5708rad)
  sketch-geometry (7):
    g0: ArcOfCircle CenterX=-7e-16 CenterY=2.8e-15 CenterZ=0 NormalX=0 NormalY=0 NormalZ=1 AngleXU=0 Radius=33 StartAngle=3.38646 EndAngle=4.42828
    g1: ArcOfCircle CenterX=-7e-16 CenterY=2.8e-15 CenterZ=0 NormalX=0 NormalY=0 NormalZ=1 AngleXU=0 Radius=33 StartAngle=4.9965 EndAngle=6.03832
    g2: LineSegment StartX=-32.0156 StartY=-8 StartZ=0 EndX=32.0156 EndY=-8 EndZ=0
    g3: LineSegment StartX=9.25 StartY=-31.6771 StartZ=0 EndX=-9.25 EndY=-31.6771 EndZ=0
    g4: Circle CenterX=-24.9 CenterY=-12.6 CenterZ=0 NormalX=0 NormalY=0 NormalZ=1 AngleXU=0 Radius=2.2
    g5: Circle CenterX=0 CenterY=-12.6 CenterZ=0 NormalX=0 NormalY=0 NormalZ=1 AngleXU=0 Radius=1.45
    g6: Circle CenterX=24.9 CenterY=-12.6 CenterZ=0 NormalX=0 NormalY=0 NormalZ=1 AngleXU=0 Radius=2.2
  constraints (15):
    c: Coincident(g0,g-3)
    c: Coincident(g0,g-4)
    c: Coincident(g1,g0)
    c: Coincident(g1,g-3)
    c: Coincident(g1,g-4)
    c: Coincident(g2,g0)
    c: Coincident(g2,g1)
    c: Coincident(g3,g1)
    c: Coincident(g3,g0)
    c: Coincident(g4,g-5)
    c: Coincident(g5,g-7)
    c: Coincident(g6,g-6)
    c: Equal(g6,g-6)
    c: Equal(g5,g-7)
    c: Equal(g4,g-5)
FEATURE [PartDesign::Pad] Pad016  label="Tapa_Habitaculo_pieza"
  BaseFeature = -> Pad
  Direction = (1,1,1)
  Length = 4.5
  Length2 = 100
  Placement = pos=(0,0,0) rot=(1,0,0;1.5708rad)
  Profile = -> Sketch037
  Type = 0
  expr: Length = <<Datos>>.grosortapa
FEATURE [Sketcher::SketchObject] Sketch039  label="SK_Pieza_pasante"
  ExternalGeometry = -> [Pad016]
  FullyConstrained = true
  MapMode = 5
  Placement = pos=(0,-1.8e-15,-8) rot=(0,0,1;3.14159rad)
  Support = -> [Pad016]
  sketch-geometry (10):
    g0: LineSegment StartX=-6.7 StartY=37.5 StartZ=0 EndX=6.7 EndY=37.5 EndZ=0
    g1: LineSegment StartX=6.7 StartY=37.5 StartZ=0 EndX=6.7 EndY=27.5 EndZ=0
    g2: LineSegment StartX=6.7 StartY=27.5 StartZ=0 EndX=-6.7 EndY=27.5 EndZ=0
    g3: LineSegment StartX=-6.7 StartY=27.5 StartZ=0 EndX=-6.7 EndY=37.5 EndZ=0
    g4: LineSegment StartX=-1.7 StartY=33 StartZ=0 EndX=1.7 EndY=33 EndZ=0
    g5: LineSegment StartX=1.7 StartY=33 StartZ=0 EndX=1.7 EndY=0 EndZ=0
    g6: LineSegment StartX=1.7 StartY=0 StartZ=0 EndX=-1.7 EndY=0 EndZ=0
    g7: LineSegment StartX=-1.7 StartY=0 StartZ=0 EndX=-1.7 EndY=33 EndZ=0
    g8: LineSegment StartX=0 StartY=0 StartZ=0 EndX=6.7 EndY=37.5 EndZ=0
    g9: LineSegment StartX=0 StartY=0 StartZ=0 EndX=-6.7 EndY=37.5 EndZ=0
  constraints (27):
    c: Coincident(g0,g1)
    c: Coincident(g1,g2)
    c: Coincident(g2,g3)
    c: Coincident(g3,g0)
    c: Horizontal(g2)
    c: Vertical(g1)
    c: Vertical(g3)
    c: DistanceY(g3,g3) = 10
    c: DistanceX(g1,g-4) = 25.3156
    c: DistanceY(g1,g-4) = 5.5
    c: Horizontal(g0)
    c: Coincident(g4,g5)
    c: Coincident(g5,g6)
    c: Coincident(g6,g7)
    c: Coincident(g7,g4)
    c: Horizontal(g4)
    c: Vertical(g5)
    c: Vertical(g7)
    c: PointOnObject(g4,g-3)
    c: PointOnObject(g5,g-1)
    c: Symmetric(g5,g6,g-2)
    c: DistanceX(g6,g6) = 3.4
    c: Coincident(g8,g-1)
    c: Coincident(g8,g0)
    c: Coincident(g9,g-1)
    c: Coincident(g9,g0)
    c: Equal(g9,g8)
FEATURE [Sketcher::SketchObject] Sketch042
  ExternalGeometry = -> [Fillet003]
  FullyConstrained = true
  MapMode = 5
  Placement = pos=(1.4e-15,33,-8) rot=(0,0,1;0rad)
  Support = -> [Fillet003]
  expr: Constraints[10] = <<Datos>>.anchoPlaca + <<Datos>>.tolerancia
  sketch-geometry (4):
    g0: LineSegment StartX=-1.7 StartY=4 StartZ=0 EndX=1.7 EndY=4 EndZ=0
    g1: LineSegment StartX=1.7 StartY=4 StartZ=0 EndX=1.7 EndY=0 EndZ=0
    g2: LineSegment StartX=1.7 StartY=0 StartZ=0 EndX=-1.7 EndY=0 EndZ=0
    g3: LineSegment StartX=-1.7 StartY=0 StartZ=0 EndX=-1.7 EndY=4 EndZ=0
  constraints (11):
    c: Coincident(g0,g1)
    c: Coincident(g1,g2)
    c: Coincident(g2,g3)
    c: Coincident(g3,g0)
    c: Horizontal(g2)
    c: Vertical(g1)
    c: Vertical(g3)
    c: PointOnObject(g0,g-3)
    c: PointOnObject(g1,g-4)
    c: Symmetric(g0,g0,g-2)
    c: DistanceX(g0,g0) = 3.4
FEATURE [PartDesign::Pocket] Pocket020  label="Con_ranura"
  BaseFeature = -> Fillet003
  Length = 2.1
  Length2 = 100
  Placement = pos=(0,33,7e-15) rot=(0,0,1;0rad)
  Profile = -> Sketch042
  Type = 0
FEATURE [Sketcher::SketchObject] Sketch044  label="SK_algo_hundido"
  ExternalGeometry = -> [ShapeBinder006]
  FullyConstrained = true
  MapMode = 5
  Placement = pos=(0,33,7e-15) rot=(1,0,0;1.5708rad)
  Support = -> [Pocket020]
  sketch-geometry (2):
    g0: ArcOfCircle CenterX=-9 CenterY=-20.249 CenterZ=0 NormalX=0 NormalY=0 NormalZ=1 AngleXU=0 Radius=9.45 StartAngle=0.309845 EndAngle=5.97334
    g1: ArcOfCircle CenterX=9 CenterY=-20.249 CenterZ=0 NormalX=0 NormalY=0 NormalZ=1 AngleXU=0 Radius=9.45 StartAngle=3.45144 EndAngle=9.11493
  constraints (6):
    c: Coincident(g0,g-3)
    c: Coincident(g1,g-4)
    c: Diameter(g1) = 18.9
    c: Equal(g1,g0)
    c: Coincident(g1,g0)
    c: Coincident(g0,g1)
FEATURE [PartDesign::Pocket] Pocket021  label="Algo_hundido"
  BaseFeature = -> Pocket020
  Length = 1.5
  Length2 = 100
  Placement = pos=(0,33,7e-15) rot=(0,0,1;0rad)
  Profile = -> Sketch044
  Type = 0
FEATURE [PartDesign::Body] Body007  label="Tapa_Pilas"
  Group = -> [ShapeBinder006,Sketch033,Pad013,Sketch034,Pad014,Fillet003,Sketch042,Pocket020,Sketch044,Pocket021]
  Origin = -> Origin007
  Tip = -> Pocket021
FEATURE [PartDesign::Pad] Pad017  label="Pieza_atornillada"
  BaseFeature = -> Pad016
  Direction = (1,1,1)
  Length = 5
  Length2 = 100
  Placement = pos=(0,0,0) rot=(1,0,0;1.5708rad)
  Profile = -> Sketch039
  Type = 0
FEATURE [Sketcher::SketchObject] Sketch045  label="SK_caja_GPS"
  ExternalGeometry = -> [Pad017]
  FullyConstrained = true
  MapMode = 5
  Placement = pos=(0,-1.8e-15,-8) rot=(0,0,1;3.14159rad)
  Support = -> [Pad017]
  expr: Constraints[11] = 2 * 10 + <<Datos>>.GPSAlto + <<Datos>>.tolerancia
  expr: Constraints[9] = <<Datos>>.GPSgrosor + <<Datos>>.tolerancia + 2 * 4
  sketch-geometry (4):
    g0: LineSegment StartX=-27.6 StartY=37.5 StartZ=0 EndX=-6.7 EndY=37.5 EndZ=0
    g1: LineSegment StartX=-6.7 StartY=37.5 StartZ=0 EndX=-6.7 EndY=-18.9 EndZ=0
    g2: LineSegment StartX=-6.7 StartY=-18.9 StartZ=0 EndX=-27.6 EndY=-18.9 EndZ=0
    g3: LineSegment StartX=-27.6 StartY=-18.9 StartZ=0 EndX=-27.6 EndY=37.5 EndZ=0
  constraints (12):
    c: Coincident(g0,g1)
    c: Coincident(g1,g2)
    c: Coincident(g2,g3)
    c: Coincident(g3,g0)
    c: Horizontal(g0)
    c: Horizontal(g2)
    c: Vertical(g1)
    c: Vertical(g3)
    c: Coincident(g0,g-5)
    c: DistanceX(g0,g0) = 20.9
    c: DistanceY(g-6,g-6) = 10  'Altura_pasante'
    c: DistanceY(g3,g3) = 56.4
FEATURE [PartDesign::Pad] Pad018  label="Caja_GPS"
  BaseFeature = -> Pad017
  Direction = (1,1,1)
  Length = 34.6
  Length2 = 100
  Placement = pos=(0,0,0) rot=(1,0,0;1.5708rad)
  Profile = -> Sketch045
  Type = 0
  expr: Length = 2 * 4 + <<Datos>>.GPSancho + <<Datos>>.tolerancia
FEATURE [Sketcher::SketchObject] Sketch040  label="SK_taladro_placa"
  AttachmentOffset = pos=(11,0,0) rot=(0,0,1;0rad)
  ExternalGeometry = -> [Pad018]
  FullyConstrained = true
  MapMode = 5
  Placement = pos=(-6.7,-2.4e-15,-11) rot=(0.707107,0,-0.707107;3.14159rad)
  Support = -> [Pad018]
  sketch-geometry (7):
    g0: LineSegment StartX=-8 StartY=37.5 StartZ=0 EndX=-3 EndY=27.5 EndZ=0
    g1: LineSegment StartX=-6.22488 StartY=30.75 StartZ=0 EndX=-4.77513 EndY=30.75 EndZ=0
    g2: LineSegment StartX=-4.77513 StartY=30.75 StartZ=0 EndX=-4.26256 EndY=31.2626 EndZ=0
    g3: LineSegment StartX=-6.22488 StartY=30.75 StartZ=0 EndX=-6.73744 EndY=31.2626 EndZ=0
    g4: LineSegment StartX=-6.73744 StartY=31.2626 StartZ=0 EndX=-4.26256 EndY=31.2626 EndZ=0
    g5: ArcOfCircle CenterX=-5.5 CenterY=32.5 CenterZ=0 NormalX=0 NormalY=0 NormalZ=1 AngleXU=0 Radius=1.75 StartAngle=5.49779 EndAngle=10.2102
    g6: ArcOfCircle CenterX=-5.5 CenterY=32.5 CenterZ=0 NormalX=0 NormalY=0 NormalZ=1 AngleXU=0 Radius=1.75 StartAngle=3.92699 EndAngle=5.17604
  constraints (18):
    c: Horizontal(g1)
    c: Coincident(g2,g1)
    c: Coincident(g3,g1)
    c: Coincident(g4,g3)
    c: Coincident(g4,g2)
    c: Horizontal(g4)
    c: Coincident(g5,g4)
    c: Tangent(g5,g2) = -1.5708
    c: Diameter(g5) = 3.5
    c: Symmetric(g0,g0,g5)
    c: Coincident(g6,g5)
    c: Coincident(g6,g3)
    c: Tangent(g1,g6)
    c: Angle(g4,g2) = 0.785398
    c: Tangent(g3,g5)
    c: Coincident(g0,g-6)
    c: Coincident(g0,g-7)
    c: PointOnObject(g6,g0)
FEATURE [PartDesign::Pocket] Pocket022  label="tornillo_pasante"
  BaseFeature = -> Pad018
  Length = 5
  Length2 = 100
  Placement = pos=(0,0,0) rot=(1,0,0;1.5708rad)
  Profile = -> Sketch040
  Type = 1
FEATURE [Sketcher::SketchObject] Sketch046  label="SK_encastre_GPS"
  ExternalGeometry = -> [Pocket022]
  FullyConstrained = true
  MapMode = 5
  Placement = pos=(0,18.9,-4.2e-15) rot=(-1,0,0;1.5708rad)
  Support = -> [Pocket022]
  expr: Constraints[9] = <<Datos>>.GPSancho + <<Datos>>.tolerancia * 1.5
  expr: Constraints[8] = <<Datos>>.GPSgrosor + <<Datos>>.tolerancia * 1.5
  sketch-geometry (5):
    g0: LineSegment StartX=10.6 StartY=4 StartZ=0 EndX=23.7 EndY=4 EndZ=0
    g1: LineSegment StartX=23.7 StartY=4 StartZ=0 EndX=23.7 EndY=-22.8 EndZ=0
    g2: LineSegment StartX=23.7 StartY=-22.8 StartZ=0 EndX=10.6 EndY=-22.8 EndZ=0
    g3: LineSegment StartX=10.6 StartY=-22.8 StartZ=0 EndX=10.6 EndY=4 EndZ=0
    g4: LineSegment StartX=17.15 StartY=-26.6 StartZ=0 EndX=17.15 EndY=8 EndZ=0
  constraints (14):
    c: Coincident(g0,g1)
    c: Coincident(g1,g2)
    c: Coincident(g2,g3)
    c: Coincident(g3,g0)
    c: Horizontal(g0)
    c: Horizontal(g2)
    c: Vertical(g1)
    c: Vertical(g3)
    c: DistanceX(g0,g0) = 13.1
    c: DistanceY(g1,g1) = 26.8
    c: Symmetric(g1,g2,g4)
    c: PointOnObject(g4,g-3)
    c: Symmetric(g-6,g-5,g4)
    c: DistanceY(g0,g-3) = 4
FEATURE [TechDraw::DrawViewPart] View001
  CoarseView = false
  Direction = (1,0,0)
  Focus = 100
  HardHidden = false
  IsoCount = 0
  IsoHidden = false
  IsoVisible = false
  LockPosition = false
  Perspective = false
  Rotation = 0
  Scale = 2
  ScaleType = 0
  SeamHidden = false
  SeamVisible = true
  SmoothHidden = false
  SmoothVisible = true
  Source = -> [Body003]
  X = 147.843
  XDirection = (0,1,0)
  Y = 132.277
FEATURE [TechDraw::DrawViewDimension] Dimension008
  Arbitrary = false
  ArbitraryTolerances = false
  EqualTolerance = true
  FormatSpec = %.2f
  FormatSpecOverTolerance = %+.2f
  FormatSpecUnderTolerance = %+.2f
  Inverted = false
  LockPosition = false
  MeasureType = 1
  OverTolerance = 0
  References2D = -> [View001]
  Rotation = 0
  ScaleType = 0
  TheoreticalExact = false
  Type = 2
  UnderTolerance = 0
  X = -125.362
  Y = 19.3
FEATURE [TechDraw::DrawViewDimension] Dimension006
  Arbitrary = false
  ArbitraryTolerances = false
  EqualTolerance = true
  FormatSpec = %.2f
  FormatSpecOverTolerance = %+.2f
  FormatSpecUnderTolerance = %+.2f
  Inverted = false
  LockPosition = false
  MeasureType = 1
  OverTolerance = 0
  References2D = -> [View001]
  Rotation = 0
  ScaleType = 0
  TheoreticalExact = false
  Type = 1
  UnderTolerance = 0
  X = -119.319
  Y = -43.8728
FEATURE [TechDraw::DrawViewDimension] Dimension005
  Arbitrary = false
  ArbitraryTolerances = false
  EqualTolerance = true
  FormatSpec = %.2f
  FormatSpecOverTolerance = %+.2f
  FormatSpecUnderTolerance = %+.2f
  Inverted = false
  LockPosition = false
  MeasureType = 1
  OverTolerance = 0
  References2D = -> [View001]
  Rotation = 0
  ScaleType = 0
  TheoreticalExact = false
  Type = 2
  UnderTolerance = 0
  X = 113.202
  Y = 0
FEATURE [TechDraw::DrawViewDimension] Dimension007
  Arbitrary = false
  ArbitraryTolerances = false
  EqualTolerance = true
  FormatSpec = %.2f
  FormatSpecOverTolerance = %+.2f
  FormatSpecUnderTolerance = %+.2f
  Inverted = false
  LockPosition = false
  MeasureType = 1
  OverTolerance = 0
  References2D = -> [View001]
  Rotation = 0
  ScaleType = 0
  TheoreticalExact = false
  Type = 2
  UnderTolerance = 0
  X = -125.437
  Y = -17.8207
FEATURE [TechDraw::DrawViewDimension] Dimension004
  Arbitrary = false
  ArbitraryTolerances = false
  EqualTolerance = true
  FormatSpec = %.2f
  FormatSpecOverTolerance = %+.2f
  FormatSpecUnderTolerance = %+.2f
  Inverted = false
  LockPosition = false
  MeasureType = 1
  OverTolerance = 0
  References2D = -> [View001]
  Rotation = 0
  ScaleType = 0
  TheoreticalExact = false
  Type = 1
  UnderTolerance = 0
  X = 0
  Y = 53.2239
FEATURE [TechDraw::DrawSVGTemplate] Template001
  EditableTexts = Designed_by_Name=Designed by Name; Drawing_number=Drawing number; FC-Date=Date; FC-SC=Scale; FC-SH=Sheet; FC-Title=Title; Subtitle=Subtitle; Weight=Weight
  Height = 210
  Orientation = 1
  Width = 297
FEATURE [TechDraw::DrawPage] Page001  label="Placa_electrónica_vista"
  KeepUpdated = true
  NextBalloonIndex = 1
  ProjectionType = 0
  Template = -> Template001
  Views = -> [View001,Dimension004,Dimension005,Dimension006,Dimension007,Dimension008]
FEATURE [TechDraw::DrawSVGTemplate] Template
  EditableTexts = Designed_by_Name=Designed by Name; Drawing_number=Drawing number; FC-Date=Date; FC-SC=Scale; FC-SH=Sheet; FC-Title=Title; Subtitle=Subtitle; Weight=Weight
  Height = 210
  Orientation = 1
  Width = 297
FEATURE [PartDesign::Pocket] Pocket023
  BaseFeature = -> Pocket022
  Length = 47.5
  Length2 = 100
  Placement = pos=(0,0,0) rot=(1,0,0;1.5708rad)
  Profile = -> Sketch046
  Type = 0
  expr: Length = <<Datos>>.GPSAlto + 11.5
FEATURE [Sketcher::SketchObject] Sketch047  label="Forma_parabolica_SK"
  ExternalGeometry = -> [Pocket023]
  FullyConstrained = true
  MapMode = 5
  Placement = pos=(27.6,0,0) rot=(0.707107,0,0.707107;3.14159rad)
  Support = -> [Pocket023]
  expr: Constraints[1] = <<Datos>>.GPSAlto + 10
  sketch-geometry (9):
    g0: LineSegment StartX=9.3 StartY=27.1 StartZ=0 EndX=9.3 EndY=-18.9 EndZ=0
    g1: LineSegment StartX=26.6 StartY=-18.9 StartZ=0 EndX=16.6 EndY=-18.9 EndZ=0
    g2: LineSegment StartX=-8 StartY=-18.9 StartZ=0 EndX=2 EndY=-18.9 EndZ=0
    g3: ArcOfParabola CenterX=9.3 CenterY=27.1 CenterZ=0 NormalX=0 NormalY=0 NormalZ=1 Focal=0.28962 AngleXU=-1.5708 StartAngle=-7.3 EndAngle=7.3
    g4: GeomPoint X=9.3 Y=26.8104 Z=0
    g5: LineSegment StartX=9.3 StartY=27.1 StartZ=0 EndX=9.3 EndY=26.8104 EndZ=0
    g6: LineSegment StartX=2 StartY=-18.9 StartZ=0 EndX=16.6 EndY=-18.9 EndZ=0
    g7: Circle CenterX=-1.5 CenterY=-14.9 CenterZ=0 NormalX=0 NormalY=0 NormalZ=1 AngleXU=0 Radius=1.5
    g8: Circle CenterX=20.1 CenterY=-14.9 CenterZ=0 NormalX=0 NormalY=0 NormalZ=1 AngleXU=0 Radius=1.5
  constraints (22):
    c: Vertical(g0)
    c: DistanceY(g0,g0) = 46
    c: Symmetric(g-4,g-3,g0)
    c: Coincident(g1,g-4)
    c: PointOnObject(g1,g-3)
    c: Coincident(g2,g-3)
    c: PointOnObject(g2,g-3)
    c: Equal(g1,g2)
    c: DistanceX(g2,g2) = 10
    c: InternalAlignment(g4,g3)
    c: Coincident(g4,g5)
    c: Coincident(g3,g5)
    c: Coincident(g3,g0)
    c: Coincident(g3,g2)
    c: Coincident(g3,g1)
    c: Coincident(g6,g3)
    c: Coincident(g6,g3)
    c: Symmetric(g8,g7,g0)
    c: DistanceX(g8,g3) = -3.5
    c: DistanceY(g8,g3) = -4
    c: Radius(g8) = 1.5
    c: Equal(g8,g7)
FEATURE [PartDesign::Pocket] Pocket024  label="Forma_parabolica"
  BaseFeature = -> Pocket023
  Length = 0
  Length2 = 100
  Placement = pos=(0,0,0) rot=(1,0,0;1.5708rad)
  Profile = -> Sketch047
  Type = 3
  UpToFace = -> Pocket023 [Face10]
FEATURE [Sketcher::SketchObject] Sketch041  label="SK_Ranura"
  FullyConstrained = false
  MapMode = 5
  Placement = pos=(0,4e-16,-3) rot=(0,0,1;3.14159rad)
  Support = -> [Pocket024]
  expr: Constraints[8] = <<Datos>>.anchoPlaca + <<Datos>>.tolerancia
  sketch-geometry (4):
    g0: LineSegment StartX=-1.7 StartY=37.5 StartZ=0 EndX=1.7 EndY=37.5 EndZ=0
    g1: LineSegment StartX=1.7 StartY=37.5 StartZ=0 EndX=1.7 EndY=-33 EndZ=0
    g2: LineSegment StartX=1.7 StartY=-33 StartZ=0 EndX=-1.7 EndY=-33 EndZ=0
    g3: LineSegment StartX=-1.7 StartY=-33 StartZ=0 EndX=-1.7 EndY=37.5 EndZ=0
  constraints (9):
    c: Coincident(g0,g1)
    c: Coincident(g1,g2)
    c: Coincident(g2,g3)
    c: Coincident(g3,g0)
    c: Horizontal(g2)
    c: Vertical(g1)
    c: Vertical(g3)
    c: Symmetric(g0,g0,g-2)
    c: DistanceX(g0,g0) = 3.4
FEATURE [PartDesign::Pocket] Pocket025  label="Ranura_placa_en_habitaculo"
  BaseFeature = -> Pocket024
  Length = 7.3
  Length2 = 100
  Placement = pos=(0,0,0) rot=(1,0,0;1.5708rad)
  Profile = -> Sketch041
  Type = 0
FEATURE [PartDesign::Fillet] Fillet006
  Base = -> Pocket025 [Edge41,Edge55,Edge28]
  BaseFeature = -> Pocket025
  Placement = pos=(0,0,0) rot=(1,0,0;1.5708rad)
  Radius = 0.5
  SupportTransform = false
FEATURE [PartDesign::Fillet] Fillet007
  Base = -> Fillet006 [Edge13,Edge80]
  BaseFeature = -> Fillet006
  Placement = pos=(0,0,0) rot=(1,0,0;1.5708rad)
  Radius = 3
  SupportTransform = false
FEATURE [PartDesign::Fillet] Fillet008
  Base = -> Fillet007 [Edge145,Edge132]
  BaseFeature = -> Fillet007
  Placement = pos=(0,0,0) rot=(1,0,0;1.5708rad)
  Radius = 3
  SupportTransform = false
FEATURE [PartDesign::Fillet] Fillet009
  Base = -> Fillet008 [Edge68,Edge64,Edge53,Edge57]
  BaseFeature = -> Fillet008
  Placement = pos=(0,0,0) rot=(1,0,0;1.5708rad)
  Radius = 2
  SupportTransform = false
FEATURE [PartDesign::Fillet] Fillet010
  Base = -> Fillet009 [Edge41]
  BaseFeature = -> Fillet009
  Placement = pos=(0,0,0) rot=(1,0,0;1.5708rad)
  Radius = 3
  SupportTransform = false
FEATURE [PartDesign::Fillet] Fillet011
  Base = -> Fillet010 [Edge98,Edge136]
  BaseFeature = -> Fillet010
  Placement = pos=(0,0,0) rot=(1,0,0;1.5708rad)
  Radius = 0.5
  SupportTransform = false
FEATURE [PartDesign::Body] Body  label="Habitaculo_Pila"
  Group = -> [Sketch,Pad,Sketch037,Pad016,Sketch039,Sketch040,Sketch041,Pad017,Sketch045,Pad018,Sketch046,Pocket022,Pocket023,Sketch047,Pocket024,Pocket025,Fillet006,Fillet007,Fillet008,Fillet009,Fillet010,Fillet011]
  Origin = -> Origin
  Tip = -> Fillet011
FEATURE [TechDraw::DrawViewPart] View
  CoarseView = false
  Direction = (1,0,0)
  Focus = 100
  HardHidden = false
  IsoCount = 0
  IsoHidden = false
  IsoVisible = false
  LockPosition = false
  Perspective = false
  Rotation = 0
  Scale = 2
  ScaleType = 0
  SeamHidden = false
  SeamVisible = true
  SmoothHidden = false
  SmoothVisible = true
  Source = -> [Body,Body004,Body005,Body006,Body007,Body009]
  X = 149.489
  XDirection = (0,1,0)
  Y = 127.509
FEATURE [TechDraw::DrawViewDimension] Dimension001
  Arbitrary = false
  ArbitraryTolerances = false
  EqualTolerance = true
  FormatSpec = %.2f
  FormatSpecOverTolerance = %+.2f
  FormatSpecUnderTolerance = %+.2f
  Inverted = false
  LockPosition = false
  MeasureType = 1
  OverTolerance = 0
  References2D = -> [View]
  Rotation = 0
  ScaleType = 0
  TheoreticalExact = false
  Type = 2
  UnderTolerance = 0
  X = 121.42
  Y = -3.24005
FEATURE [TechDraw::DrawViewDimension] Dimension
  Arbitrary = false
  ArbitraryTolerances = false
  EqualTolerance = true
  FormatSpec = %.2f
  FormatSpecOverTolerance = %+.2f
  FormatSpecUnderTolerance = %+.2f
  Inverted = false
  LockPosition = false
  MeasureType = 1
  OverTolerance = 0
  References2D = -> [View]
  Rotation = 0
  ScaleType = 0
  TheoreticalExact = false
  Type = 1
  UnderTolerance = 0
  X = 0
  Y = 55.3173
FEATURE [TechDraw::DrawViewDimension] Dimension003
  Arbitrary = false
  ArbitraryTolerances = false
  EqualTolerance = true
  FormatSpec = %.2f
  FormatSpecOverTolerance = %+.2f
  FormatSpecUnderTolerance = %+.2f
  Inverted = false
  LockPosition = false
  MeasureType = 1
  OverTolerance = 0
  References2D = -> [View]
  Rotation = 0
  ScaleType = 0
  TheoreticalExact = false
  Type = 1
  UnderTolerance = 0
  X = -3.18545
  Y = 4.37559
FEATURE [TechDraw::DrawViewDimension] Dimension002
  Arbitrary = false
  ArbitraryTolerances = false
  EqualTolerance = true
  FormatSpec = %.2f
  FormatSpecOverTolerance = %+.2f
  FormatSpecUnderTolerance = %+.2f
  Inverted = false
  LockPosition = false
  MeasureType = 1
  OverTolerance = 0
  References2D = -> [View]
  Rotation = 0
  ScaleType = 0
  TheoreticalExact = false
  Type = 1
  UnderTolerance = 0
  X = -128.662
  Y = 69.0849
FEATURE [TechDraw::DrawPage] Page  label="Vista_general"
  KeepUpdated = true
  NextBalloonIndex = 1
  ProjectionType = 0
  Template = -> Template
  Views = -> [View,Dimension,Dimension001,Dimension002,Dimension003]
